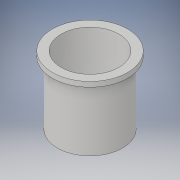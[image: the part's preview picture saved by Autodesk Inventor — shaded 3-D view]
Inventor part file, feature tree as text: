
AUTODESK INVENTOR PART (.ipt)
format: ipt  version: 2017 (Build 210142000, 142)  size: 143,872 bytes
history: native  units: in
note: dims shown in document units (in); Inventor stores cm internally (conversion verified against a paired STEP export)
features: revolve x1, sketch x1
ambient origin geometry x8: Origin, YZ Plane, XZ Plane, XY Plane, X Axis, Y Axis, Z Axis, Center Point
bodies: Body1 (feature_tree)
feature tree (2):
  revolve  "Revolution3"  [1 undecoded]
  sketch  "Sketch1"  dims[d0=1.13in d1=3.75in d2=0.25in d3=0.1718in d5=1.0in d6=1.0in d7=90.0deg d8=0.5in d9=15.0deg d11=0.25in d12=1.25in d13=0.25in d15=0.25in d16=0.5in d17=0.5in d18=0.5in d19=2.5in d20=0.5in d22=0.375in d23=0.25in d25=0.234in d26=15.0deg d29=90.0deg d30=3.0in]
note: 1 required parameter value undecoded (feature->parameter linkage not recoverable at this tier; creation-order binding heuristic only, values carry confidence <= 0.55)
